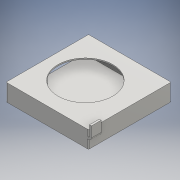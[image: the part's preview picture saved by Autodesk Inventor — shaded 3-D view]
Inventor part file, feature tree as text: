
AUTODESK INVENTOR PART (.ipt)
format: ipt  version: 2016 (Build 200138000, 138)  size: 175,104 bytes
history: native  units: mm
features: sketch x3, extrude x2, sweep x1, fillet x1, projected_geometry x1
ambient origin geometry x8: Origin, YZ Plane, XZ Plane, XY Plane, X Axis, Y Axis, Z Axis, Center Point
bodies: Solid1 (feature_tree), body (feature_tree)
feature tree (8):
  extrude  "outlet"  Depth=11.3mm
  extrude  "Extrusion3"  Depth=5.4mm
  sweep  "Sweep1"
  fillet  "Fillet1"  Radius=0.5mm
  sketch  "Sketch2"  dims[d0=17.0mm d1=11.3mm]
  projected_geometry  "Projected Loop1"
  sketch  "Sketch3"  dims[d2=3.5mm d3=0.0mm d4=5.4mm]
  sketch  "Sketch4"  dims[d5=0.84mm d6=0.25mm d7=0.5mm d8=15.0mm d9=0.0mm d10=15.0mm d11=0.0mm d12=3.5mm d14=9.15mm d15=1.0mm d16=0.6mm d17=2.0mm d18=0.4mm d19=0.0mm d20=0.0mm d21=0.2mm d22=0.65mm]
